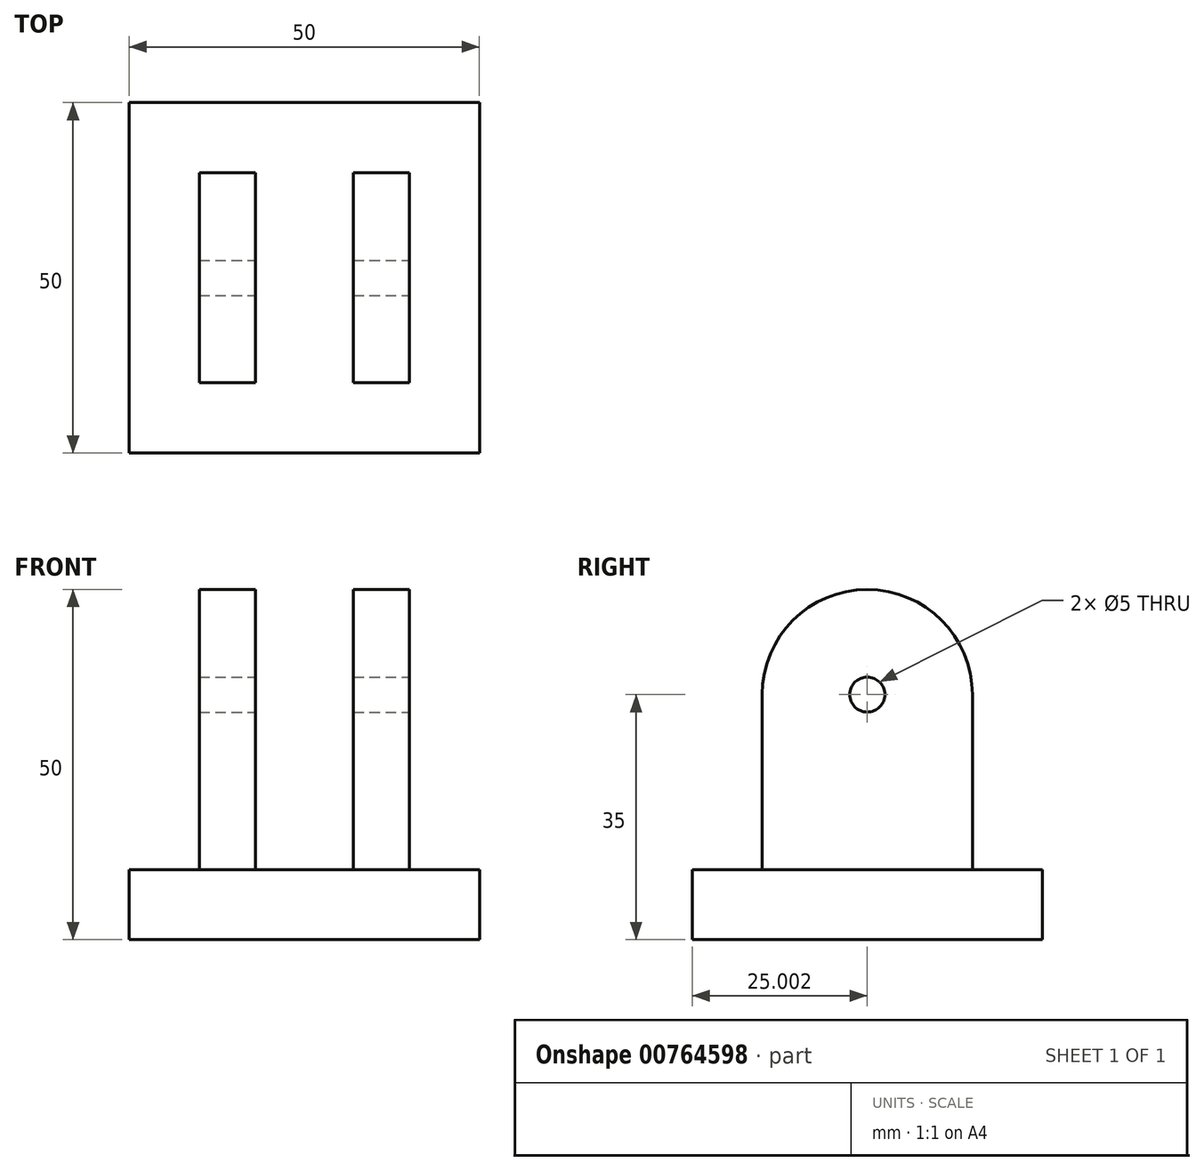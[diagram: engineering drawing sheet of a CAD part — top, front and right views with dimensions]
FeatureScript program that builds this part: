
annotation { "Feature Type Name" : "Feature", "Feature Type Description" : "" }
export const myFeature = defineFeature(function(context is Context, id is Id, definition is map)
    precondition{}
    {
        {
            var Q0;
            Q0=qCreatedBy(makeId("Top.planeOp"),FACE);
            var sketch = newSketch(context, id + "F0", { "sketchPlane" : qUnion([Q0])});
            skLineSegment(sketch, "E0.bottom", {"start": v(-44.05, -44.69) * mm, "end": v(5.95, -44.69) * mm});
            skLineSegment(sketch, "E0.top", {"start": v(-44.05, 5.31) * mm, "end": v(5.95, 5.31) * mm});
            skLineSegment(sketch, "E0.left", {"start": v(-44.05, -44.69) * mm, "end": v(-44.05, 5.31) * mm});
            skLineSegment(sketch, "E0.right", {"start": v(5.95, -44.69) * mm, "end": v(5.95, 5.31) * mm});
            skSolve(sketch);
        }
        {
            var Q0;
            Q0=makeQuery(id+"F0.imprint","IMPRINT",FACE,{"disambiguationData":[TD([[makeQuery(id+"F0.imprint","IMPRINT",EDGE,{"derivedFrom":sQuery(id+"F0.wireOp",EDGE,"E0.bottom")}),1.0]])]});
            extrude(context, id + "F1", {"entities" : qUnion([Q0]), "depth" : 10 * mm, "offsetDistance" : 25 * mm});
        }
        {
            var Q0;
            Q0=makeQuery(id+"F1.opExtrude","CAP_FACE",FACE,{"disambiguationData":[OSD([sQuery(id+"F0.wireOp",EDGE,"E0.bottom"),sQuery(id+"F0.wireOp",EDGE,"E0.top"),sQuery(id+"F0.wireOp",EDGE,"E0.left"),sQuery(id+"F0.wireOp",EDGE,"E0.right")])],"isStart":false});
            var sketch = newSketch(context, id + "F2", { "sketchPlane" : qUnion([Q0])});
            skLineSegment(sketch, "E1.bottom", {"start": v(-34.05, -4.69) * mm, "end": v(-26.05, -4.69) * mm});
            skLineSegment(sketch, "E1.top", {"start": v(-34.05, -34.69) * mm, "end": v(-26.05, -34.69) * mm});
            skLineSegment(sketch, "E1.left", {"start": v(-34.05, -4.69) * mm, "end": v(-34.05, -34.69) * mm});
            skLineSegment(sketch, "E1.right", {"start": v(-26.05, -4.69) * mm, "end": v(-26.05, -34.69) * mm});
            skSolve(sketch);
        }
        {
            var Q0;
            Q0=makeQuery(id+"F2.imprint","IMPRINT",FACE,{"disambiguationData":[TD([[makeQuery(id+"F2.imprint","IMPRINT",EDGE,{"derivedFrom":sQuery(id+"F2.wireOp",EDGE,"E1.bottom")}),1.0]])]});
            var sketch = newSketch(context, id + "F3", { "sketchPlane" : qUnion([Q0])});
            skLineSegment(sketch, "E2.bottom", {"start": v(-12.05, -4.69) * mm, "end": v(-4.05, -4.69) * mm});
            skLineSegment(sketch, "E2.top", {"start": v(-12.05, -34.69) * mm, "end": v(-4.05, -34.69) * mm});
            skLineSegment(sketch, "E2.left", {"start": v(-12.05, -4.69) * mm, "end": v(-12.05, -34.69) * mm});
            skLineSegment(sketch, "E2.right", {"start": v(-4.05, -4.69) * mm, "end": v(-4.05, -34.69) * mm});
            skSolve(sketch);
        }
        {
            var Q0;
            Q0=makeQuery(id+"F3.imprint","IMPRINT",FACE,{"disambiguationData":[TD([[makeQuery(id+"F3.imprint","IMPRINT",EDGE,{"derivedFrom":sQuery(id+"F3.wireOp",EDGE,"E2.bottom")}),-1.0]])]});
            extrude(context, id + "F4", {"entities" : qUnion([Q0]), "operationType" : NewBodyOperationType.ADD, "depth" : 40 * mm, "offsetDistance" : 25 * mm});
        }
        {
            var Q0;
            Q0=makeQuery(id+"F2.imprint","IMPRINT",FACE,{"disambiguationData":[TD([[makeQuery(id+"F2.imprint","IMPRINT",EDGE,{"derivedFrom":sQuery(id+"F2.wireOp",EDGE,"E1.bottom")}),-1.0]])]});
            extrude(context, id + "F5", {"entities" : qUnion([Q0]), "operationType" : NewBodyOperationType.ADD, "depth" : 40 * mm, "offsetDistance" : 25 * mm});
        }
        {
            var Q0;
            Q0=makeQuery(id+"F4.opExtrude","CAP_EDGE",EDGE,{"disambiguationData":[OSD([sQuery(id+"F3.wireOp",EDGE,"E2.bottom")])],"isStart":false});
            var Q1;
            Q1=makeQuery(id+"F5.opExtrude","CAP_EDGE",EDGE,{"disambiguationData":[OSD([sQuery(id+"F2.wireOp",EDGE,"E1.bottom")])],"isStart":false});
            var Q2;
            Q2=makeQuery(id+"F4.opExtrude","CAP_EDGE",EDGE,{"disambiguationData":[OSD([sQuery(id+"F3.wireOp",EDGE,"E2.top")])],"isStart":false});
            var Q3;
            Q3=makeQuery(id+"F5.opExtrude","CAP_EDGE",EDGE,{"disambiguationData":[OSD([sQuery(id+"F2.wireOp",EDGE,"E1.top")])],"isStart":false});
            fillet(context, id + "F6", {"entities" : qUnion([Q0, Q1, Q2, Q3]), "radius" : 15 * mm, "tangentPropagation" : true, "allowEdgeOverflow" : false});
        }
        {
            var Q0;
            Q0=makeQuery(id+"F4.opExtrude","SWEPT_FACE",FACE,{"disambiguationData":[OSD([sQuery(id+"F3.wireOp",EDGE,"E2.right")])]});
            var sketch = newSketch(context, id + "F7", { "sketchPlane" : qUnion([Q0])});
            skPoint(sketch, "E3", {"position": v(-19.69, 35) * mm});
            skSolve(sketch);
        }
        {
            var Q0;
            Q0=sQuery(id+"F7.wireOp",VERTEX,"E3");
            var Q1;
            Q1=makeQuery(id+"F1.opExtrude","SWEPT_BODY",BODY,{"disambiguationData":[OSD([sQuery(id+"F0.wireOp",EDGE,"E0.bottom"),sQuery(id+"F0.wireOp",EDGE,"E0.top"),sQuery(id+"F0.wireOp",EDGE,"E0.left"),sQuery(id+"F0.wireOp",EDGE,"E0.right")])]});
            hole(context, id + "F8", {"style" : HoleStyle.SIMPLE, "endStyle" : HoleEndStyle.THROUGH, "holeDiameter" : 5 * mm, "majorDiameter" : 5 * mm, "isTappedThrough" : true, "tappedDepth" : 12 * mm, "tapClearance" : 3, "locations" : qUnion([Q0]), "scope" : qUnion([Q1])});
        }
    });
